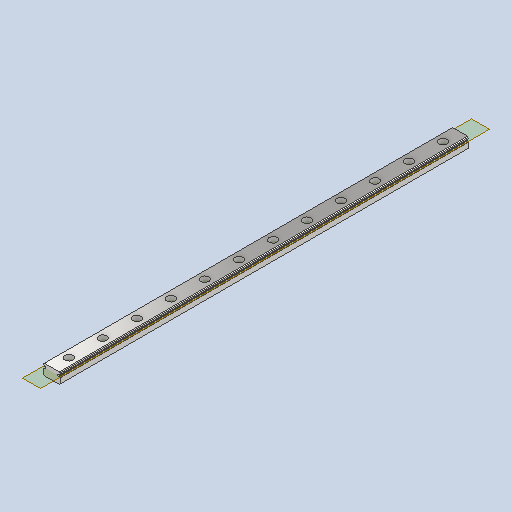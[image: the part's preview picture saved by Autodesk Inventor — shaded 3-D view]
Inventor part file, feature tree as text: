
AUTODESK INVENTOR PART (.ipt)
format: ipt  version: 2024 (Build 280153000, 153)  size: 329,728 bytes
history: native  units: mm
features: pattern_linear x1, plane x1, other x1
ambient origin geometry x8: Origin, YZ Plane, XZ Plane, XY Plane, X Axis, Y Axis, Z Axis, Center Point
bodies: Solid1 (feature_tree)
feature tree (3):
  pattern_linear  "Rectangular Pattern1"  Count1=3  [1 undecoded]
  plane  "Work Plane1"
  other  "LPattern1"
note: 1 required parameter value undecoded (feature->parameter linkage not recoverable at this tier; creation-order binding heuristic only, values carry confidence <= 0.55)
